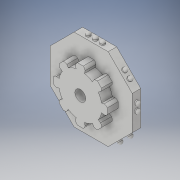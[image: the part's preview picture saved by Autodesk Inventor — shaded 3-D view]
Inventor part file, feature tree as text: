
AUTODESK INVENTOR PART (.ipt)
format: ipt  version: 2017 (Build 210142000, 142)  size: 352,256 bytes
history: native  units: in
note: dims shown in document units (in); Inventor stores cm internally (conversion verified against a paired STEP export)
features: sketch x12, extrude x10, fillet x7, pattern_circular x1
ambient origin geometry x8: Origin, YZ Plane, XZ Plane, XY Plane, X Axis, Y Axis, Z Axis, Center Point
bodies: Solid1 (feature_tree)
feature tree (30):
  extrude  "Extrusion1"  Depth=0.1181in TaperAngle=0.0deg
  extrude  "Extrusion2"  Depth=0.1in
  fillet  "Fillet1"  Radius=0.1in
  sketch  "Sketch3"  dims[d8=0.063in d9=0.063in d10=0.059in]
  sketch  "Sketch4"  dims[d11=0.0472in d12=0.0in d13=0.0315in d24=0.059in]
  sketch  "Sketch5"  dims[d25=0.063in d26=0.1in d27=0.1in d28=0.063in d29=0.063in d31=0.0575in d32=0.059in d34=0.0in d35=0.059in]
  sketch  "Sketch6"  dims[d36=0.059in]
  sketch  "Sketch7"  dims[d40=0.063in d41=0.1in d42=0.1in d43=0.063in d44=0.063in d46=0.059in d47=0.0in d48=0.059in d49=0.059in d50=0.0in d51=0.0in]
  sketch  "Sketch8"  dims[d70=0.063in d71=0.1in d72=0.1in d73=0.063in d74=0.063in d76=0.059in d77=0.0in d78=0.059in d79=0.059in d81=0.0in d82=0.0in]
  sketch  "Sketch9"  dims[d83=0.063in d84=0.1in d85=0.1in d86=0.063in d87=0.063in d89=0.059in d90=0.059in d91=0.059in d92=0.0in d93=0.0in d94=0.0in d95=0.0in]
  extrude  "Extrusion6"  Depth=0.063in
  fillet  "Fillet5"  Radius=0.059in
  extrude  "Extrusion7"  Depth=0.0315in
  fillet  "Fillet6"  Radius=0.059in
  extrude  "Extrusion8"  TaperAngle=0.0deg  [1 undecoded]
  fillet  "Fillet7"  Radius=0.059in
  extrude  "Extrusion9"  TaperAngle=0.0deg  [1 undecoded]
  fillet  "Fillet8"  [1 undecoded]
  extrude  "Extrusion10"  TaperAngle=0.0deg  [1 undecoded]
  fillet  "Fillet9"  [1 undecoded]
  extrude  "Extrusion11"  TaperAngle=0.0deg  [1 undecoded]
  fillet  "Fillet10"  [1 undecoded]
  extrude  "Extrusion14"  Depth=0.0315in
  pattern_circular  "Circular Pattern4"  [2 undecoded]
  extrude  "Extrusion15"  Depth=0.15in TaperAngle=0.0deg
  sketch  "Sketch13"  dims[d125=0.0472in d126=0.0in d127=0.0315in d128=0.0472in d129=0.0in d130=0.0315in d131=0.0472in d132=0.0in d133=0.0315in d134=0.0472in d135=0.0in d136=0.0315in d137=0.0472in d138=0.0in d139=0.0315in d148=0.6in d154=12.5984in d156=360.0deg d161=0.04in d162=0.04in d163=0.15in d164=0.0in d165=3.1496in d166=360.0deg d168=0.075in d169=0.236in d170=0.236in d171=0.236in d172=0.236in d173=0.236in d175=0.236in d176=0.236in d177=0.15in d178=1.0in d179=0.0in]
  sketch  "Sketch1"  dims[d2=0.4724in d3=0.1181in d4=0.0in]
  sketch  "Sketch2"  dims[d5=0.063in d6=0.1in d7=0.1in]
  sketch  "Sketch11"  dims[d96=0.063in d97=0.1in d98=0.1in d99=0.063in d100=0.063in d102=0.059in d103=0.059in d104=0.059in d105=0.0in d106=0.0in d107=0.0in d108=0.0in]
  sketch  "Sketch12"  dims[d109=0.063in d110=0.1in d111=0.1in d112=0.063in d113=0.063in d115=0.059in d116=0.059in d117=0.059in d118=0.0in d119=0.0in d120=0.0in d121=0.0in d122=0.0472in d123=0.0in d124=0.0315in]
note: 9 required parameter values undecoded (feature->parameter linkage not recoverable at this tier; creation-order binding heuristic only, values carry confidence <= 0.55)
